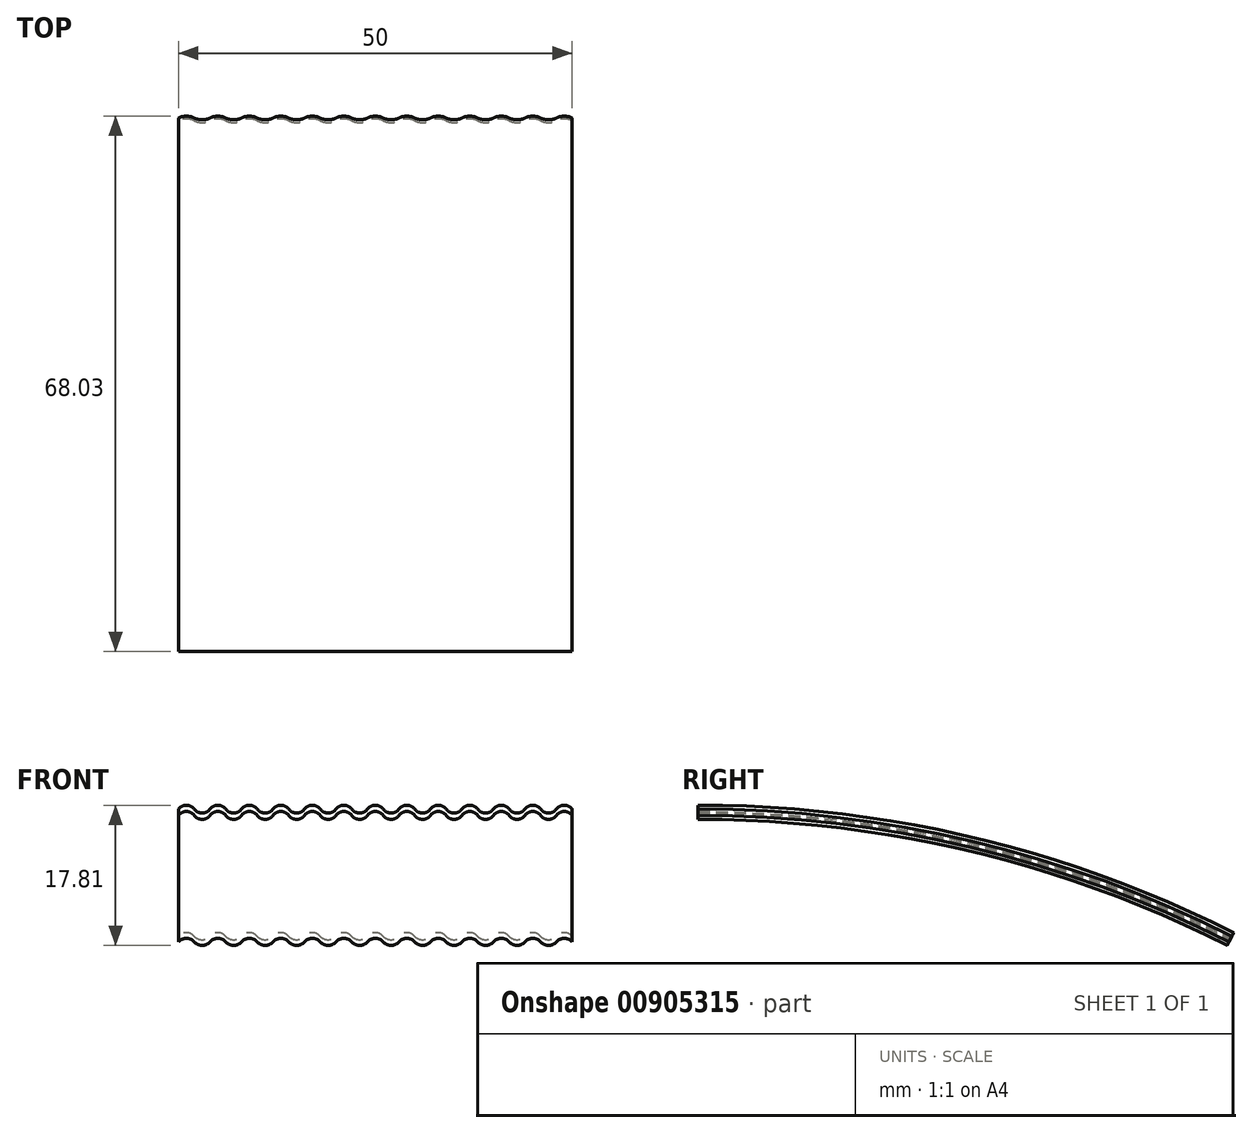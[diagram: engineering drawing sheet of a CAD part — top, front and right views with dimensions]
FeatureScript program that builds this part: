
annotation { "Feature Type Name" : "Feature", "Feature Type Description" : "" }
export const myFeature = defineFeature(function(context is Context, id is Id, definition is map)
    precondition{}
    {
        {
            var Q0;
            Q0=qCreatedBy(makeId("Front.planeOp"),FACE);
            var sketch = newSketch(context, id + "F0", { "sketchPlane" : qUnion([Q0])});
            skArc(sketch, "E0", {"start": v(-19, -0.4) * mm, "mid": v(-20, 0.1) * mm, "end": v(-21, -0.4) * mm});
            skArc(sketch, "E1", {"start": v(-23, -0.4) * mm, "mid": v(-22, -0.9) * mm, "end": v(-21, -0.4) * mm});
            skArc(sketch, "E2", {"start": v(-23, -0.4) * mm, "mid": v(-24, 0.1) * mm, "end": v(-25, -0.4) * mm});
            skArc(sketch, "E3", {"start": v(5, -0.4) * mm, "mid": v(6, -0.9) * mm, "end": v(7, -0.4) * mm});
            skArc(sketch, "E4", {"start": v(9, -0.4) * mm, "mid": v(8, 0.1) * mm, "end": v(7, -0.4) * mm});
            skArc(sketch, "E5", {"start": v(9, -0.4) * mm, "mid": v(10, -0.9) * mm, "end": v(11, -0.4) * mm});
            skArc(sketch, "E6", {"start": v(13, -0.4) * mm, "mid": v(12, 0.1) * mm, "end": v(11, -0.4) * mm});
            skArc(sketch, "E7", {"start": v(13, -0.4) * mm, "mid": v(14, -0.9) * mm, "end": v(15, -0.4) * mm});
            skArc(sketch, "E8", {"start": v(17, -0.4) * mm, "mid": v(16, 0.1) * mm, "end": v(15, -0.4) * mm});
            skArc(sketch, "E9", {"start": v(25, -0.4) * mm, "mid": v(24, 0.1) * mm, "end": v(23, -0.4) * mm});
            skArc(sketch, "E10", {"start": v(21, -0.4) * mm, "mid": v(22, -0.9) * mm, "end": v(23, -0.4) * mm});
            skArc(sketch, "E11", {"start": v(21, -0.4) * mm, "mid": v(20, 0.1) * mm, "end": v(19, -0.4) * mm});
            skArc(sketch, "E12", {"start": v(17, -0.4) * mm, "mid": v(18, -0.9) * mm, "end": v(19, -0.4) * mm});
            skArc(sketch, "E13", {"start": v(5, -0.4) * mm, "mid": v(4, 0.1) * mm, "end": v(3, -0.4) * mm});
            skArc(sketch, "E14", {"start": v(1, -0.4) * mm, "mid": v(2, -0.9) * mm, "end": v(3, -0.4) * mm});
            skArc(sketch, "E15", {"start": v(1, -0.4) * mm, "mid": v(0, 0.1) * mm, "end": v(-1, -0.4) * mm});
            skArc(sketch, "E16", {"start": v(-3, -0.4) * mm, "mid": v(-2, -0.9) * mm, "end": v(-1, -0.4) * mm});
            skArc(sketch, "E17", {"start": v(-3, -0.4) * mm, "mid": v(-4, 0.1) * mm, "end": v(-5, -0.4) * mm});
            skArc(sketch, "E18", {"start": v(-7, -0.4) * mm, "mid": v(-6, -0.9) * mm, "end": v(-5, -0.4) * mm});
            skArc(sketch, "E19", {"start": v(-7, -0.4) * mm, "mid": v(-8, 0.1) * mm, "end": v(-9, -0.4) * mm});
            skArc(sketch, "E20", {"start": v(-11, -0.4) * mm, "mid": v(-10, -0.9) * mm, "end": v(-9, -0.4) * mm});
            skArc(sketch, "E21", {"start": v(-11, -0.4) * mm, "mid": v(-12, 0.1) * mm, "end": v(-13, -0.4) * mm});
            skArc(sketch, "E22", {"start": v(-15, -0.4) * mm, "mid": v(-14, -0.9) * mm, "end": v(-13, -0.4) * mm});
            skArc(sketch, "E23", {"start": v(-15, -0.4) * mm, "mid": v(-16, 0.1) * mm, "end": v(-17, -0.4) * mm});
            skArc(sketch, "E24", {"start": v(-19, -0.4) * mm, "mid": v(-18, -0.9) * mm, "end": v(-17, -0.4) * mm});
            skArc(sketch, "E25", {"start": v(-19, 0.4) * mm, "mid": v(-20, 0.9) * mm, "end": v(-21, 0.4) * mm});
            skArc(sketch, "E26", {"start": v(-23, 0.4) * mm, "mid": v(-22, -0.1) * mm, "end": v(-21, 0.4) * mm});
            skArc(sketch, "E27", {"start": v(-23, 0.4) * mm, "mid": v(-24, 0.9) * mm, "end": v(-25, 0.4) * mm});
            skArc(sketch, "E28", {"start": v(5, 0.4) * mm, "mid": v(6, -0.1) * mm, "end": v(7, 0.4) * mm});
            skArc(sketch, "E29", {"start": v(9, 0.4) * mm, "mid": v(8, 0.9) * mm, "end": v(7, 0.4) * mm});
            skArc(sketch, "E30", {"start": v(9, 0.4) * mm, "mid": v(10, -0.1) * mm, "end": v(11, 0.4) * mm});
            skArc(sketch, "E31", {"start": v(13, 0.4) * mm, "mid": v(12, 0.9) * mm, "end": v(11, 0.4) * mm});
            skArc(sketch, "E32", {"start": v(13, 0.4) * mm, "mid": v(14, -0.1) * mm, "end": v(15, 0.4) * mm});
            skArc(sketch, "E33", {"start": v(17, 0.4) * mm, "mid": v(16, 0.9) * mm, "end": v(15, 0.4) * mm});
            skArc(sketch, "E34", {"start": v(25, 0.4) * mm, "mid": v(24, 0.9) * mm, "end": v(23, 0.4) * mm});
            skArc(sketch, "E35", {"start": v(21, 0.4) * mm, "mid": v(22, -0.1) * mm, "end": v(23, 0.4) * mm});
            skArc(sketch, "E36", {"start": v(21, 0.4) * mm, "mid": v(20, 0.9) * mm, "end": v(19, 0.4) * mm});
            skArc(sketch, "E37", {"start": v(17, 0.4) * mm, "mid": v(18, -0.1) * mm, "end": v(19, 0.4) * mm});
            skArc(sketch, "E38", {"start": v(5, 0.4) * mm, "mid": v(4, 0.9) * mm, "end": v(3, 0.4) * mm});
            skArc(sketch, "E39", {"start": v(1, 0.4) * mm, "mid": v(2, -0.1) * mm, "end": v(3, 0.4) * mm});
            skArc(sketch, "E40", {"start": v(1, 0.4) * mm, "mid": v(0, 0.9) * mm, "end": v(-1, 0.4) * mm});
            skArc(sketch, "E41", {"start": v(-3, 0.4) * mm, "mid": v(-2, -0.1) * mm, "end": v(-1, 0.4) * mm});
            skArc(sketch, "E42", {"start": v(-3, 0.4) * mm, "mid": v(-4, 0.9) * mm, "end": v(-5, 0.4) * mm});
            skArc(sketch, "E43", {"start": v(-7, 0.4) * mm, "mid": v(-6, -0.1) * mm, "end": v(-5, 0.4) * mm});
            skArc(sketch, "E44", {"start": v(-7, 0.4) * mm, "mid": v(-8, 0.9) * mm, "end": v(-9, 0.4) * mm});
            skArc(sketch, "E45", {"start": v(-11, 0.4) * mm, "mid": v(-10, -0.1) * mm, "end": v(-9, 0.4) * mm});
            skArc(sketch, "E46", {"start": v(-11, 0.4) * mm, "mid": v(-12, 0.9) * mm, "end": v(-13, 0.4) * mm});
            skArc(sketch, "E47", {"start": v(-15, 0.4) * mm, "mid": v(-14, -0.1) * mm, "end": v(-13, 0.4) * mm});
            skArc(sketch, "E48", {"start": v(-15, 0.4) * mm, "mid": v(-16, 0.9) * mm, "end": v(-17, 0.4) * mm});
            skArc(sketch, "E49", {"start": v(-19, 0.4) * mm, "mid": v(-18, -0.1) * mm, "end": v(-17, 0.4) * mm});
            skLineSegment(sketch, "E50", {"start": v(-25, 0.4) * mm, "end": v(-25, -0.4) * mm});
            skLineSegment(sketch, "E51", {"start": v(25, 0.4) * mm, "end": v(25, -0.4) * mm});
            skSolve(sketch);
        }
        {
            var Q0;
            Q0=qCreatedBy(makeId("Right.planeOp"),FACE);
            var sketch = newSketch(context, id + "F1", { "sketchPlane" : qUnion([Q0])});
            skLineSegment(sketch, "E52", {"start": v(0, 0) * mm, "end": v(0, -150) * mm, "construction": true});
            skArc(sketch, "E53", {"start": v(0, 0) * mm, "mid": v(34.76, -4.08) * mm, "end": v(67.62, -16.1) * mm});
            skSolve(sketch);
        }
        {
            var Q0;
            Q0=makeQuery(id+"F0.imprint","IMPRINT",FACE,{"disambiguationData":[TD([[makeQuery(id+"F0.imprint","IMPRINT",EDGE,{"derivedFrom":sQuery(id+"F0.wireOp",EDGE,"E0")}),-1.0]])]});
            var Q1;
            Q1=sQuery(id+"F1.wireOp",EDGE,"E53");
            sweep(context, id + "F2", {"profiles" : qUnion([Q0]), "path" : qUnion([Q1])});
        }
    });
